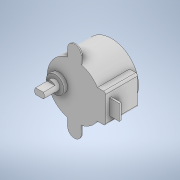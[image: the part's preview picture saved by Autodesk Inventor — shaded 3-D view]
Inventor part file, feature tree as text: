
AUTODESK INVENTOR PART (.ipt)
format: ipt  version: 2021 (Build 250183000, 183)  size: 187,904 bytes
history: native  units: mm
features: extrude x7, sketch x7, fillet x2
ambient origin geometry x8: Origin, YZ Plane, XZ Plane, XY Plane, X Axis, Y Axis, Z Axis, Center Point
bodies: Solid1 (feature_tree)
feature tree (16):
  extrude  "Extrusion1"  Depth=19.0mm TaperAngle=0.0deg
  extrude  "Extrusion2"  Depth=10.0mm
  fillet  "Fillet1"  Radius=16.0mm
  extrude  "Extrusion3"  Depth=16.5mm TaperAngle=0.0deg
  extrude  "Extrusion4"  Depth=9.0mm
  extrude  "Extrusion5"  Depth=8.0mm
  extrude  "Extrusion6"  Depth=5.0mm
  extrude  "Extrusion7"  Depth=3.0mm
  fillet  "Fillet2"  Radius=1.5mm
  sketch  "Sketch1"  dims[d0=28.0mm d1=19.0mm d2=0.0mm]
  sketch  "Sketch2"  dims[d3=15.0mm d4=10.0mm d5=16.0mm]
  sketch  "Sketch3"  dims[d6=7.5mm d7=16.5mm d8=0.0mm]
  sketch  "Sketch4"  dims[d9=1.0mm d10=9.0mm]
  sketch  "Sketch5"  dims[d11=0.0mm d12=8.0mm]
  sketch  "Sketch6"  dims[d13=2.0mm d14=0.0mm d15=5.0mm]
  sketch  "Sketch7"  dims[d16=8.0mm d17=0.0mm d18=3.0mm d19=1.5mm d20=6.0mm d21=0.0mm d22=2.0mm d23=1.0mm d24=3.5mm d25=3.5mm d26=5.0mm d27=0.0mm d28=7.0mm d29=7.0mm d30=3.5mm d31=2.0mm d32=7.0mm d33=7.0mm d34=2.0mm d35=3.5mm d36=0.5mm d37=0.0mm d38=3.5mm]
